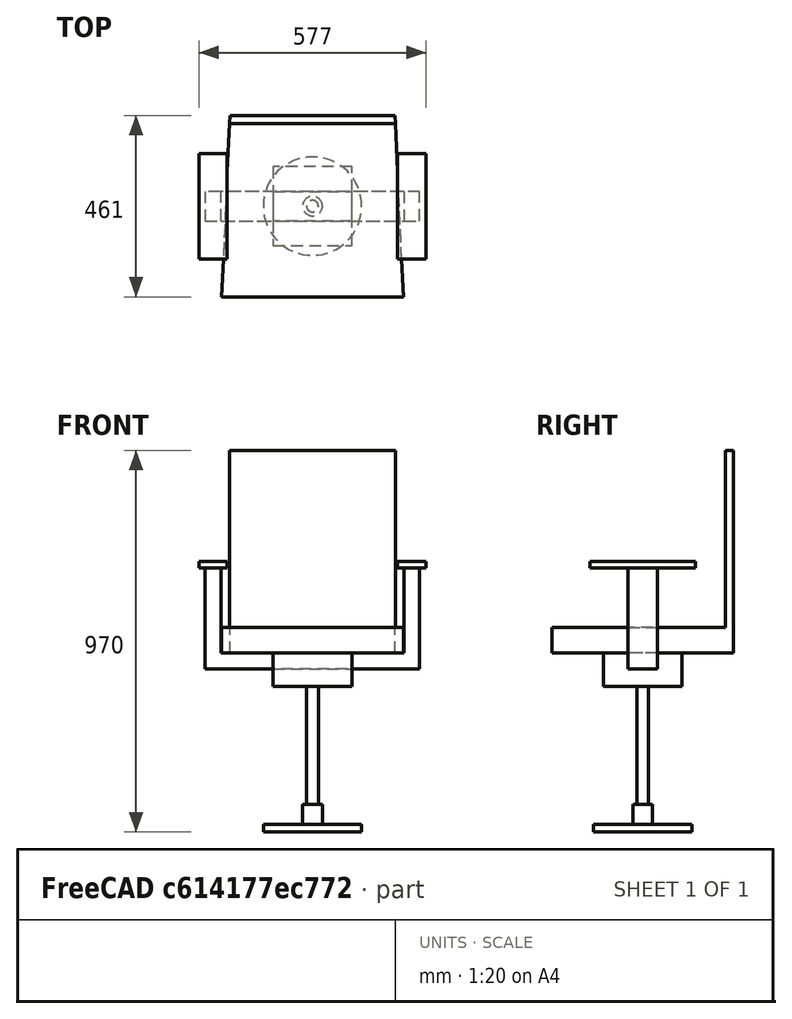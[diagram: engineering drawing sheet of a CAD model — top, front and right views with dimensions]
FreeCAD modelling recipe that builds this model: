
FCSTD DOCUMENT  (FreeCAD 1.0R39109 (Git))
Label: chair02_00501
License: All rights reserved
LicenseURL: https://en.wikipedia.org/wiki/All_rights_reserved
objects: TechDraw::DrawViewDimension×11, Sketcher::SketchObject×10, PartDesign::Pad×10, TechDraw::DrawViewAnnotation×9, PartDesign::Body×5, PartDesign::ShapeBinder×4, TechDraw::DrawSVGTemplate×3, TechDraw::DrawProjGroupItem×3, TechDraw::DrawPage×3, TechDraw::DrawViewSection×3, App::Part×1
note: 79 computed .brp shape members not serialized (recipe doc carries the construction recipe); baked Part::Feature solids carry a one-line shape summary decoded from their .brp

FEATURE [Sketcher::SketchObject] Sketch
  ArcFitTolerance = 1e-06
  AttachmentSupport = -> [XY_Plane]
  FullyConstrained = true
  MakeInternals = false
  MapMode = 5
  sketch-geometry (1):
    g0: Circle CenterX=0 CenterY=0 CenterZ=0 NormalX=0 NormalY=0 NormalZ=1 AngleXU=0 Radius=125
  constraints (2):
    c: Diameter(g0) = 250
    c: Coincident(g0,g-1)
FEATURE [PartDesign::Pad] Pad
  Direction = (0,0,1)
  Length = 20
  Length2 = 10
  Profile = -> Sketch
  ReferenceAxis = -> Sketch [N_Axis]
  Refine = true
  Suppressed = false
  Type = 0
FEATURE [Sketcher::SketchObject] Sketch001
  ArcFitTolerance = 1e-06
  AttachmentSupport = -> [Pad]
  FullyConstrained = true
  MakeInternals = false
  MapMode = 5
  Placement = pos=(0,0,20) rot=(0,0,1;0rad)
  sketch-geometry (1):
    g0: Circle CenterX=0 CenterY=0 CenterZ=0 NormalX=0 NormalY=0 NormalZ=1 AngleXU=0 Radius=25
  constraints (2):
    c: Diameter(g0) = 50
    c: Coincident(g0,g-1)
FEATURE [PartDesign::Pad] Pad001
  BaseFeature = -> Pad
  Direction = (0,0,1)
  Length = 50
  Length2 = 10
  Profile = -> Sketch001
  ReferenceAxis = -> Sketch001 [N_Axis]
  Refine = true
  Suppressed = false
  Type = 0
FEATURE [PartDesign::Body] Body  label="Body1"
  AllowCompound = false
  Group = -> [Sketch,Pad,Sketch001,Pad001]
  Origin = -> Origin
  Tip = -> Pad001
FEATURE [PartDesign::ShapeBinder] CopyPad001  label="Body2_Sketch_P.lane"
  Placement = pos=(0,0,50) rot=(0,0,1;0rad)
  TraceSupport = false
FEATURE [Sketcher::SketchObject] Sketch002
  ArcFitTolerance = 1e-06
  AttachmentSupport = -> [CopyPad001]
  FullyConstrained = true
  MakeInternals = false
  MapMode = 5
  Placement = pos=(0,0,70) rot=(0,0,1;0rad)
  sketch-geometry (1):
    g0: Circle CenterX=0 CenterY=0 CenterZ=0 NormalX=0 NormalY=0 NormalZ=1 AngleXU=0 Radius=15
  constraints (2):
    c: Diameter(g0) = 30
    c: Coincident(g0,g-1)
FEATURE [PartDesign::Pad] Pad002
  Direction = (0,0,1)
  Length = 300
  Length2 = 10
  Placement = pos=(0,0,50) rot=(0,0,1;0rad)
  Profile = -> Sketch002
  ReferenceAxis = -> Sketch002 [N_Axis]
  Refine = true
  Suppressed = false
  Type = 0
FEATURE [PartDesign::Body] Body001  label="Body2"
  AllowCompound = false
  Group = -> [CopyPad001,Sketch002,Pad002]
  Origin = -> Origin001
  Tip = -> Pad002
FEATURE [PartDesign::ShapeBinder] CopyPad002  label="Body3_Sketch_Plane"
  Placement = pos=(0,0,300) rot=(0,0,1;0rad)
  TraceSupport = false
FEATURE [Sketcher::SketchObject] Sketch003
  ArcFitTolerance = 1e-06
  AttachmentSupport = -> [CopyPad002]
  FullyConstrained = true
  MakeInternals = false
  MapMode = 5
  Placement = pos=(0,0,370) rot=(0,0,1;0rad)
  sketch-geometry (5):
    g0: LineSegment StartX=-100 StartY=-100 StartZ=0 EndX=100 EndY=-100 EndZ=0
    g1: LineSegment StartX=100 StartY=-100 StartZ=0 EndX=100 EndY=100 EndZ=0
    g2: LineSegment StartX=100 StartY=100 StartZ=0 EndX=-100 EndY=100 EndZ=0
    g3: LineSegment StartX=-100 StartY=100 StartZ=0 EndX=-100 EndY=-100 EndZ=0
    g4: GeomPoint [constr] X=0 Y=0 Z=0
  constraints (12):
    c: Coincident(g0,g1)
    c: Coincident(g1,g2)
    c: Coincident(g2,g3)
    c: Coincident(g3,g0)
    c: Horizontal(g0)
    c: Horizontal(g2)
    c: Vertical(g1)
    c: Vertical(g3)
    c: Symmetric(g2,g0,g4)
    c: Distance(g1,g3) = 200
    c: Distance(g0,g2) = 200
    c: Coincident(g4,g-1)
FEATURE [PartDesign::Pad] Pad003
  Direction = (0,0,1)
  Length = 45
  Length2 = 10
  Placement = pos=(0,0,300) rot=(0,0,1;0rad)
  Profile = -> Sketch003
  ReferenceAxis = -> Sketch003 [N_Axis]
  Refine = true
  Suppressed = false
  Type = 0
FEATURE [PartDesign::ShapeBinder] CopyPad003  label="Body4_Sketch_Plane"
  Placement = pos=(0,0,45) rot=(0,0,1;0rad)
  TraceSupport = false
FEATURE [Sketcher::SketchObject] Sketch004
  ArcFitTolerance = 1e-06
  AttachmentSupport = -> [CopyPad003]
  FullyConstrained = true
  MakeInternals = false
  MapMode = 5
  Placement = pos=(0,0,415) rot=(0,0,1;0rad)
  sketch-geometry (5):
    g0: LineSegment StartX=-272.5 StartY=-37.5 StartZ=0 EndX=272.5 EndY=-37.5 EndZ=0
    g1: LineSegment StartX=272.5 StartY=-37.5 StartZ=0 EndX=272.5 EndY=37.5 EndZ=0
    g2: LineSegment StartX=272.5 StartY=37.5 StartZ=0 EndX=-272.5 EndY=37.5 EndZ=0
    g3: LineSegment StartX=-272.5 StartY=37.5 StartZ=0 EndX=-272.5 EndY=-37.5 EndZ=0
    g4: GeomPoint [constr] X=0 Y=0 Z=0
  constraints (12):
    c: Coincident(g0,g1)
    c: Coincident(g1,g2)
    c: Coincident(g2,g3)
    c: Coincident(g3,g0)
    c: Horizontal(g0)
    c: Horizontal(g2)
    c: Vertical(g1)
    c: Vertical(g3)
    c: Symmetric(g2,g0,g4)
    c: Distance(g1,g3) = 545
    c: Distance(g0,g2) = 75
    c: Coincident(g4,g-1)
FEATURE [PartDesign::Pad] Pad004
  Direction = (0,0,1)
  Length = 40
  Length2 = 10
  Placement = pos=(0,0,45) rot=(0,0,1;0rad)
  Profile = -> Sketch004
  ReferenceAxis = -> Sketch004 [N_Axis]
  Refine = true
  Suppressed = false
  Type = 0
FEATURE [Sketcher::SketchObject] Sketch005
  ArcFitTolerance = 1e-06
  AttachmentSupport = -> [Pad004]
  ExternalGeometry = -> [Pad004]
  FullyConstrained = true
  MakeInternals = false
  MapMode = 5
  Placement = pos=(0,0,455) rot=(0,0,1;0rad)
  sketch-geometry (8):
    g0: LineSegment StartX=-272.5 StartY=37.5 StartZ=0 EndX=-272.5 EndY=-37.5 EndZ=0
    g1: LineSegment StartX=-272.5 StartY=-37.5 StartZ=0 EndX=-232.5 EndY=-37.5 EndZ=0
    g2: LineSegment StartX=-232.5 StartY=-37.5 StartZ=0 EndX=-232.5 EndY=37.5 EndZ=0
    g3: LineSegment StartX=-232.5 StartY=37.5 StartZ=0 EndX=-272.5 EndY=37.5 EndZ=0
    g4: LineSegment StartX=272.5 StartY=37.5 StartZ=0 EndX=232.5 EndY=37.5 EndZ=0
    g5: LineSegment StartX=232.5 StartY=37.5 StartZ=0 EndX=232.5 EndY=-37.5 EndZ=0
    g6: LineSegment StartX=232.5 StartY=-37.5 StartZ=0 EndX=272.5 EndY=-37.5 EndZ=0
    g7: LineSegment StartX=272.5 StartY=-37.5 StartZ=0 EndX=272.5 EndY=37.5 EndZ=0
  constraints (22):
    c: Coincident(g0,g1)
    c: Coincident(g1,g2)
    c: Coincident(g2,g3)
    c: Coincident(g3,g0)
    c: Vertical(g0)
    c: Vertical(g2)
    c: Horizontal(g1)
    c: Horizontal(g3)
    c: Coincident(g0,g-3)
    c: PointOnObject(g1,g-4)
    c: DistanceX(g3,g3) = 40
    c: Coincident(g4,g5)
    c: Coincident(g5,g6)
    c: Coincident(g6,g7)
    c: Coincident(g7,g4)
    c: Horizontal(g4)
    c: Horizontal(g6)
    c: Vertical(g5)
    c: Vertical(g7)
    c: Coincident(g4,g-3)
    c: PointOnObject(g5,g-4)
    c: Equal(g4,g3)
FEATURE [PartDesign::Pad] Pad005
  BaseFeature = -> Pad004
  Direction = (0,0,1)
  Length = 216
  Length2 = 10
  Placement = pos=(0,0,45) rot=(0,0,1;0rad)
  Profile = -> Sketch005
  ReferenceAxis = -> Sketch005 [N_Axis]
  Refine = true
  Suppressed = false
  Type = 0
FEATURE [Sketcher::SketchObject] Sketch006
  ArcFitTolerance = 1e-06
  AttachmentSupport = -> [Pad005]
  ExternalGeometry = -> [Pad005]
  FullyConstrained = true
  MakeInternals = false
  MapMode = 5
  Placement = pos=(0,0,671) rot=(0,0,1;0rad)
  sketch-geometry (16):
    g0: LineSegment StartX=-288.5 StartY=134 StartZ=0 EndX=-288.5 EndY=-134 EndZ=0
    g1: LineSegment StartX=-288.5 StartY=-134 StartZ=0 EndX=-216.5 EndY=-134 EndZ=0
    g2: LineSegment StartX=-216.5 StartY=-134 StartZ=0 EndX=-216.5 EndY=134 EndZ=0
    g3: LineSegment StartX=-216.5 StartY=134 StartZ=0 EndX=-288.5 EndY=134 EndZ=0
    g4: LineSegment StartX=216.5 StartY=134 StartZ=0 EndX=216.5 EndY=-134 EndZ=0
    g5: LineSegment StartX=216.5 StartY=-134 StartZ=0 EndX=288.5 EndY=-134 EndZ=0
    g6: LineSegment StartX=288.5 StartY=-134 StartZ=0 EndX=288.5 EndY=134 EndZ=0
    g7: LineSegment StartX=288.5 StartY=134 StartZ=0 EndX=216.5 EndY=134 EndZ=0
    g8: LineSegment [constr] StartX=-272.5 StartY=37.5 StartZ=0 EndX=-232.5 EndY=-37.5 EndZ=0
    g9: LineSegment [constr] StartX=-252.5 StartY=0 StartZ=0 EndX=-272.5 EndY=-37.5 EndZ=0
    g10: LineSegment [constr] StartX=232.5 StartY=37.5 StartZ=0 EndX=272.5 EndY=-37.5 EndZ=0
    g11: LineSegment [constr] StartX=272.5 StartY=37.5 StartZ=0 EndX=252.5 EndY=0 EndZ=0
    g12: LineSegment [constr] StartX=-216.5 StartY=134 StartZ=0 EndX=-288.5 EndY=-134 EndZ=0
    g13: LineSegment [constr] StartX=-288.5 StartY=134 StartZ=0 EndX=-252.5 EndY=0 EndZ=0
    g14: LineSegment [constr] StartX=216.5 StartY=134 StartZ=0 EndX=288.5 EndY=-134 EndZ=0
    g15: LineSegment [constr] StartX=288.5 StartY=134 StartZ=0 EndX=252.5 EndY=0 EndZ=0
  constraints (38):
    c: Coincident(g0,g1)
    c: Coincident(g1,g2)
    c: Coincident(g2,g3)
    c: Coincident(g3,g0)
    c: Vertical(g0)
    c: Vertical(g2)
    c: Horizontal(g1)
    c: Horizontal(g3)
    c: Coincident(g4,g5)
    c: Coincident(g5,g6)
    c: Coincident(g6,g7)
    c: Coincident(g7,g4)
    c: Vertical(g4)
    c: Vertical(g6)
    c: Horizontal(g5)
    c: Horizontal(g7)
    c: Equal(g7,g3)
    c: Equal(g2,g4)
    c: DistanceX(g3,g3) = 72
    c: Coincident(g8,g-4)
    c: Coincident(g8,g-3)
    c: Coincident(g9,g-4)
    c: Coincident(g10,g-5)
    c: Coincident(g10,g-6)
    c: Coincident(g11,g-6)
    c: Symmetric(g10,g10,g11)
    c: Symmetric(g8,g8,g9)
    c: Coincident(g12,g2)
    c: Coincident(g12,g0)
    c: Coincident(g13,g0)
    c: Symmetric(g12,g12,g13)
    c: Coincident(g9,g13)
    c: Coincident(g14,g4)
    c: Coincident(g14,g5)
    c: Coincident(g15,g6)
    c: Symmetric(g14,g14,g15)
    c: Coincident(g15,g11)
    c: DistanceY(g2,g2) = 268
FEATURE [PartDesign::Pad] Pad006
  BaseFeature = -> Pad005
  Direction = (0,0,1)
  Length = 17
  Length2 = 10
  Placement = pos=(0,0,45) rot=(0,0,1;0rad)
  Profile = -> Sketch006
  ReferenceAxis = -> Sketch006 [N_Axis]
  Refine = true
  Suppressed = false
  Type = 0
FEATURE [PartDesign::Body] Body003  label="Body4"
  AllowCompound = false
  Group = -> [CopyPad003,Sketch004,Pad004,Sketch005,Pad005,Sketch006,Pad006]
  Origin = -> Origin003
  Tip = -> Pad006
FEATURE [PartDesign::ShapeBinder] CopyPad006  label="Body5_Sketch_Plane"
  Placement = pos=(0,0,45) rot=(0,0,1;0rad)
  TraceSupport = false
FEATURE [Sketcher::SketchObject] Sketch009
  ArcFitTolerance = 1e-06
  AttachmentSupport = -> [Pad003]
  ExternalGeometry = -> [Pad003]
  FullyConstrained = true
  MakeInternals = false
  MapMode = 5
  Placement = pos=(0,0,415) rot=(0,0,1;0rad)
  sketch-geometry (8):
    g0: LineSegment StartX=-100 StartY=100 StartZ=0 EndX=-100 EndY=37.5 EndZ=0
    g1: LineSegment StartX=-100 StartY=37.5 StartZ=0 EndX=100 EndY=37.5 EndZ=0
    g2: LineSegment StartX=100 StartY=37.5 StartZ=0 EndX=100 EndY=100 EndZ=0
    g3: LineSegment StartX=100 StartY=100 StartZ=0 EndX=-100 EndY=100 EndZ=0
    g4: LineSegment StartX=100 StartY=-100 StartZ=0 EndX=100 EndY=-37.5 EndZ=0
    g5: LineSegment StartX=100 StartY=-37.5 StartZ=0 EndX=-100 EndY=-37.5 EndZ=0
    g6: LineSegment StartX=-100 StartY=-37.5 StartZ=0 EndX=-100 EndY=-100 EndZ=0
    g7: LineSegment StartX=-100 StartY=-100 StartZ=0 EndX=100 EndY=-100 EndZ=0
  constraints (21):
    c: Coincident(g0,g1)
    c: Coincident(g1,g2)
    c: Coincident(g2,g3)
    c: Coincident(g3,g0)
    c: Vertical(g0)
    c: Vertical(g2)
    c: Horizontal(g1)
    c: Horizontal(g3)
    c: Coincident(g0,g-3)
    c: PointOnObject(g1,g-4)
    c: Coincident(g4,g5)
    c: Coincident(g5,g6)
    c: Coincident(g6,g7)
    c: Coincident(g7,g4)
    c: Vertical(g6)
    c: Horizontal(g5)
    c: Horizontal(g7)
    c: Coincident(g4,g-4)
    c: PointOnObject(g5,g-3)
    c: DistanceY(g4,g1) = 75
    c: Symmetric(g1,g4,g-1)
FEATURE [PartDesign::Pad] Pad009
  BaseFeature = -> Pad003
  Direction = (0,0,1)
  Length = 40
  Length2 = 10
  Placement = pos=(0,0,300) rot=(0,0,1;0rad)
  Profile = -> Sketch009
  ReferenceAxis = -> Sketch009 [N_Axis]
  Refine = true
  Suppressed = false
  Type = 0
FEATURE [PartDesign::Body] Body002  label="Body3"
  AllowCompound = false
  Group = -> [CopyPad002,Sketch003,Pad003,Sketch009,Pad009]
  Origin = -> Origin002
  Tip = -> Pad009
FEATURE [Sketcher::SketchObject] Sketch007
  ArcFitTolerance = 1e-06
  AttachmentSupport = -> [CopyPad006]
  FullyConstrained = true
  MakeInternals = false
  MapMode = 5
  Placement = pos=(0,0,455) rot=(0,0,1;0rad)
  sketch-geometry (8):
    g0: LineSegment StartX=-210 StartY=230.5 StartZ=0 EndX=-231 EndY=-230.5 EndZ=0
    g1: LineSegment StartX=-231 StartY=-230.5 StartZ=0 EndX=231 EndY=-230.5 EndZ=0
    g2: LineSegment StartX=231 StartY=-230.5 StartZ=0 EndX=210 EndY=230.5 EndZ=0
    g3: LineSegment StartX=210 StartY=230.5 StartZ=0 EndX=-210 EndY=230.5 EndZ=0
    g4: LineSegment [constr] StartX=210 StartY=230.5 StartZ=0 EndX=2.84e-14 EndY=0 EndZ=0
    g5: LineSegment [constr] StartX=2.84e-14 StartY=0 StartZ=0 EndX=-210 EndY=230.5 EndZ=0
    g6: LineSegment [constr] StartX=210 StartY=230.5 StartZ=0 EndX=210 EndY=0 EndZ=0
    g7: LineSegment [constr] StartX=231 StartY=-230.5 StartZ=0 EndX=231 EndY=0 EndZ=0
  constraints (20):
    c: Coincident(g2,g1)
    c: DistanceX(g1,g1) = 462
    c: DistanceX(g3,g3) = 420
    c: Coincident(g1,g0)
    c: Symmetric(g2,g0,g-2)
    c: Coincident(g2,g3)
    c: Coincident(g3,g0)
    c: Coincident(g4,g2)
    c: Coincident(g4,g-1)
    c: Coincident(g5,g4)
    c: Coincident(g5,g0)
    c: DistanceY(g2,g2) = 461
    c: Coincident(g6,g2)
    c: PointOnObject(g6,g-1)
    c: Vertical(g6)
    c: Coincident(g7,g1)
    c: PointOnObject(g7,g-1)
    c: Vertical(g7)
    c: Equal(g7,g6)
    c: Symmetric(g1,g0,g-2)
FEATURE [PartDesign::Pad] Pad007
  Direction = (0,0,1)
  Length = 65
  Length2 = 10
  Placement = pos=(0,0,45) rot=(0,0,1;0rad)
  Profile = -> Sketch007
  ReferenceAxis = -> Sketch007 [N_Axis]
  Refine = true
  Suppressed = false
  Type = 0
FEATURE [Sketcher::SketchObject] Sketch008
  ArcFitTolerance = 1e-06
  AttachmentSupport = -> [Pad007]
  ExternalGeometry = -> [Pad007]
  FullyConstrained = true
  MakeInternals = false
  MapMode = 5
  Placement = pos=(0,0,520) rot=(0,0,1;0rad)
  sketch-geometry (4):
    g0: LineSegment StartX=-210 StartY=230.5 StartZ=0 EndX=210 EndY=230.5 EndZ=0
    g1: LineSegment StartX=-210 StartY=230.5 StartZ=0 EndX=-210.957 EndY=209.5 EndZ=0
    g2: LineSegment StartX=-210.957 StartY=209.5 StartZ=0 EndX=210.957 EndY=209.5 EndZ=0
    g3: LineSegment StartX=210 StartY=230.5 StartZ=0 EndX=210.957 EndY=209.5 EndZ=0
  constraints (10):
    c: Coincident(g0,g-3)
    c: Coincident(g0,g-4)
    c: Coincident(g1,g0)
    c: PointOnObject(g1,g-3)
    c: Coincident(g2,g1)
    c: PointOnObject(g2,g-4)
    c: Horizontal(g2)
    c: Coincident(g3,g0)
    c: Coincident(g3,g2)
    c: DistanceY(g1,g1) = 21
FEATURE [PartDesign::Pad] Pad008
  BaseFeature = -> Pad007
  Direction = (0,0,1)
  Length = 450
  Length2 = 10
  Placement = pos=(0,0,45) rot=(0,0,1;0rad)
  Profile = -> Sketch008
  ReferenceAxis = -> Sketch008 [N_Axis]
  Refine = true
  Suppressed = false
  Type = 0
FEATURE [PartDesign::Body] Body004  label="Body5"
  AllowCompound = false
  Group = -> [CopyPad006,Sketch007,Pad007,Sketch008,Pad008]
  Origin = -> Origin004
  Tip = -> Pad008
FEATURE [App::Part] Part  label="chair02"
  Group = -> [Body,Body001,Body002,Body003,Body004]
  Origin = -> Origin005
FEATURE [TechDraw::DrawSVGTemplate] Template  label="テンプレート"
  Height = 210
  Orientation = 1
  Template = <userpath>/AppData/Local/Programs/FreeCAD 1.0/data/Mod/TechDraw/Templates/A4_Landscape_blank.svg
  Width = 297
FEATURE [TechDraw::DrawProjGroupItem] View
  CoarseView = false
  Direction = (0,0,1)
  Focus = 100
  HardHidden = true
  IsoCount = 0
  IsoHidden = false
  IsoVisible = false
  LockPosition = false
  Perspective = false
  Rotation = 0
  RotationVector = (1,0,0)
  Scale = 0.333333
  ScaleType = 2
  ScrubCount = 1
  SeamHidden = false
  SeamVisible = false
  SmoothHidden = false
  SmoothVisible = true
  Source = -> [Part]
  Type = 0
  X = 131.425
  XDirection = (1,0,0)
  Y = 107.897
FEATURE [TechDraw::DrawViewDimension] Dimension  label="寸法"
  AngleOverride = false
  Arbitrary = false
  ArbitraryTolerances = false
  BoxCorners = (2) [(-96.1666,-76.8333,0),(96.1666,76.8333,0)]
  EqualTolerance = true
  ExtensionAngle = 0
  FormatSpec = %.2w
  FormatSpecOverTolerance = %+.2w
  FormatSpecUnderTolerance = %+.2w
  Inverted = false
  LineAngle = 0
  LockPosition = false
  MeasureType = 1
  OverTolerance = 0
  References2D = -> [View]
  Rotation = 0
  Scale = 0.2
  ScaleType = 2
  TheoreticalExact = false
  Type = 1
  UnderTolerance = 0
  X = 0
  Y = 93.9298
FEATURE [TechDraw::DrawViewDimension] Dimension001  label="寸法001"
  AngleOverride = false
  Arbitrary = false
  ArbitraryTolerances = false
  BoxCorners = (2) [(-96.1666,-76.8333,0),(96.1666,76.8333,0)]
  EqualTolerance = true
  ExtensionAngle = 0
  FormatSpec = %.2w
  FormatSpecOverTolerance = %+.2w
  FormatSpecUnderTolerance = %+.2w
  Inverted = false
  LineAngle = 0
  LockPosition = false
  MeasureType = 1
  OverTolerance = 0
  References2D = -> [View]
  Rotation = 0
  Scale = 0.2
  ScaleType = 2
  TheoreticalExact = false
  Type = 2
  UnderTolerance = 0
  X = 135.701
  Y = 0
FEATURE [TechDraw::DrawViewDimension] Dimension002  label="寸法002"
  AngleOverride = false
  Arbitrary = false
  ArbitraryTolerances = false
  BoxCorners = (2) [(-96.1666,-76.8333,0),(96.1666,76.8333,0)]
  EqualTolerance = true
  ExtensionAngle = 0
  FormatSpec = %.2w
  FormatSpecOverTolerance = %+.2w
  FormatSpecUnderTolerance = %+.2w
  Inverted = false
  LineAngle = 0
  LockPosition = false
  MeasureType = 1
  OverTolerance = 0
  References2D = -> [View]
  Rotation = 0
  Scale = 0.2
  ScaleType = 2
  TheoreticalExact = false
  Type = 2
  UnderTolerance = 0
  X = 113.57
  Y = 61.6706
FEATURE [TechDraw::DrawViewDimension] Dimension003  label="寸法003"
  AngleOverride = false
  Arbitrary = false
  ArbitraryTolerances = false
  BoxCorners = (2) [(-96.1666,-76.8333,0),(96.1666,76.8333,0)]
  EqualTolerance = true
  ExtensionAngle = 0
  FormatSpec = %.2w
  FormatSpecOverTolerance = %+.2w
  FormatSpecUnderTolerance = %+.2w
  Inverted = false
  LineAngle = 0
  LockPosition = false
  MeasureType = 1
  OverTolerance = 0
  References2D = -> [View]
  Rotation = 0
  Scale = 0.2
  ScaleType = 2
  TheoreticalExact = false
  Type = 2
  UnderTolerance = 0
  X = 125.233
  Y = 0.063601
FEATURE [TechDraw::DrawViewDimension] Dimension004  label="寸法004"
  AngleOverride = false
  Arbitrary = false
  ArbitraryTolerances = false
  BoxCorners = (2) [(-96.1666,-76.8333,0),(96.1666,76.8333,0)]
  EqualTolerance = true
  ExtensionAngle = 0
  FormatSpec = %.2w
  FormatSpecOverTolerance = %+.2w
  FormatSpecUnderTolerance = %+.2w
  Inverted = false
  LineAngle = 0
  LockPosition = false
  MeasureType = 1
  OverTolerance = 0
  References2D = -> [View]
  Rotation = 0
  Scale = 0.2
  ScaleType = 2
  TheoreticalExact = false
  Type = 1
  UnderTolerance = 0
  X = -84.1666
  Y = 58.5053
FEATURE [TechDraw::DrawViewDimension] Dimension005  label="寸法005"
  AngleOverride = false
  Arbitrary = false
  ArbitraryTolerances = false
  BoxCorners = (2) [(-96.1666,-76.8333,0),(96.1666,76.8333,0)]
  EqualTolerance = true
  ExtensionAngle = 0
  FormatSpec = %.2w
  FormatSpecOverTolerance = %+.2w
  FormatSpecUnderTolerance = %+.2w
  Inverted = false
  LineAngle = 0
  LockPosition = false
  MeasureType = 1
  OverTolerance = 0
  References2D = -> [View]
  Rotation = 0
  Scale = 0.2
  ScaleType = 2
  TheoreticalExact = false
  Type = 2
  UnderTolerance = 0
  X = -108.801
  Y = 0
FEATURE [TechDraw::DrawViewDimension] Dimension006  label="寸法006"
  AngleOverride = false
  Arbitrary = false
  ArbitraryTolerances = false
  BoxCorners = (2) [(-96.1666,-76.8333,0),(96.1666,76.8333,0)]
  EqualTolerance = true
  ExtensionAngle = 0
  FormatSpec = %.2w
  FormatSpecOverTolerance = %+.2w
  FormatSpecUnderTolerance = %+.2w
  Inverted = false
  LineAngle = 0
  LockPosition = false
  MeasureType = 1
  OverTolerance = 0
  References2D = -> [View]
  Rotation = 0
  Scale = 0.2
  ScaleType = 2
  TheoreticalExact = false
  Type = 1
  UnderTolerance = 0
  X = 0
  Y = -83.8244
FEATURE [TechDraw::DrawPage] Page  label="用紙"
  KeepUpdated = true
  NextBalloonIndex = 1
  ProjectionType = 0
  Template = -> Template
  Views = -> [View,Dimension,Dimension001,Dimension002,Dimension003,Dimension004,Dimension005,Dimension006]
FEATURE [TechDraw::DrawSVGTemplate] Template001  label="テンプレート001"
  Height = 210
  Orientation = 1
  Template = <userpath>/AppData/Local/Programs/FreeCAD 1.0/data/Mod/TechDraw/Templates/A4_Landscape_blank.svg
  Width = 297
FEATURE [TechDraw::DrawSVGTemplate] Template002  label="テンプレート002"
  Height = 210
  Orientation = 1
  Template = <userpath>/AppData/Local/Programs/FreeCAD 1.0/data/Mod/TechDraw/Templates/A4_Landscape_blank.svg
  Width = 297
FEATURE [TechDraw::DrawProjGroupItem] View001
  CoarseView = false
  Direction = (0,-1,0)
  Focus = 100
  HardHidden = true
  IsoCount = 0
  IsoHidden = false
  IsoVisible = false
  LockPosition = false
  Perspective = false
  Rotation = 0
  RotationVector = (1,0,0)
  Scale = 0.2
  ScaleType = 2
  ScrubCount = 1
  SeamHidden = false
  SeamVisible = false
  SmoothHidden = false
  SmoothVisible = true
  Source = -> [Part]
  Type = 0
  X = 72.2264
  XDirection = (1,0,0)
  Y = 108.632
FEATURE [TechDraw::DrawViewSection] SectionView  label="セクション  - "
  BaseView = -> View001
  CoarseView = false
  CutSurfaceDisplay = 2
  Direction = (1e-16,0,1)
  FileGeomPattern = <userpath>\AppData\Local\Programs\FreeCAD 1.0\data\Mod/TechDraw/PAT/FCPAT.pat
  FileHatchPattern = <userpath>\AppData\Local\Programs\FreeCAD 1.0\data\Mod/TechDraw/Patterns/simple.svg
  Focus = 100
  FuseBeforeCut = false
  HardHidden = true
  HatchOffset = (0,0,0)
  HatchRotation = 0
  HatchScale = 1
  IsoCount = 0
  IsoHidden = false
  IsoVisible = false
  LockPosition = false
  NameGeomPattern = Diamond
  Perspective = false
  Rotation = 0
  Scale = 0.15
  ScaleType = 2
  ScrubCount = 1
  SeamHidden = false
  SeamVisible = false
  SectionDirection = 4
  SectionLineStretch = 1
  SectionNormal = (1e-16,0,1)
  SectionOrigin = (0,0,581)
  SmoothHidden = false
  SmoothVisible = true
  Source = -> [Part]
  TrimAfterCut = false
  UsePreviousCut = false
  X = 215.858
  XDirection = (1,0,-1e-16)
  Y = 166.085
FEATURE [TechDraw::DrawViewSection] SectionView001  label="セクション001  - "
  BaseView = -> View001
  CoarseView = false
  CutSurfaceDisplay = 2
  Direction = (1e-16,0,1)
  FileGeomPattern = <userpath>\AppData\Local\Programs\FreeCAD 1.0\data\Mod/TechDraw/PAT/FCPAT.pat
  FileHatchPattern = <userpath>\AppData\Local\Programs\FreeCAD 1.0\data\Mod/TechDraw/Patterns/simple.svg
  Focus = 100
  FuseBeforeCut = false
  HardHidden = true
  HatchOffset = (0,0,0)
  HatchRotation = 0
  HatchScale = 1
  IsoCount = 0
  IsoHidden = false
  IsoVisible = false
  LockPosition = false
  NameGeomPattern = Diamond
  Perspective = false
  Rotation = 0
  Scale = 0.15
  ScaleType = 2
  ScrubCount = 1
  SeamHidden = false
  SeamVisible = false
  SectionDirection = 4
  SectionLineStretch = 1
  SectionNormal = (1e-16,0,1)
  SectionOrigin = (0,0,437)
  SmoothHidden = false
  SmoothVisible = true
  Source = -> [Part]
  TrimAfterCut = false
  UsePreviousCut = false
  X = 215.086
  XDirection = (1,0,-1e-16)
  Y = 92.3168
FEATURE [TechDraw::DrawViewSection] SectionView002  label="セクション002  - "
  BaseView = -> View001
  CoarseView = false
  CutSurfaceDisplay = 2
  Direction = (1e-16,0,1)
  FileGeomPattern = <userpath>\AppData\Local\Programs\FreeCAD 1.0\data\Mod/TechDraw/PAT/FCPAT.pat
  FileHatchPattern = <userpath>\AppData\Local\Programs\FreeCAD 1.0\data\Mod/TechDraw/Patterns/simple.svg
  Focus = 100
  FuseBeforeCut = false
  HardHidden = true
  HatchOffset = (0,0,0)
  HatchRotation = 0
  HatchScale = 1
  IsoCount = 0
  IsoHidden = false
  IsoVisible = false
  LockPosition = false
  NameGeomPattern = Diamond
  Perspective = false
  Rotation = 0
  Scale = 0.15
  ScaleType = 2
  ScrubCount = 1
  SeamHidden = false
  SeamVisible = false
  SectionDirection = 4
  SectionLineStretch = 1
  SectionNormal = (1e-16,0,1)
  SectionOrigin = (0,0,200)
  SmoothHidden = false
  SmoothVisible = true
  Source = -> [Part]
  TrimAfterCut = false
  UsePreviousCut = false
  X = 214.868
  XDirection = (1,0,-1e-16)
  Y = 24.434
FEATURE [TechDraw::DrawViewDimension] Dimension014  label="寸法014"
  AngleOverride = false
  Arbitrary = false
  ArbitraryTolerances = false
  BoxCorners = (2) [(-18.75,-18.75,0),(18.75,18.75,0)]
  EqualTolerance = true
  ExtensionAngle = 0
  FormatSpec = ⌀%.2w
  FormatSpecOverTolerance = %+.2w
  FormatSpecUnderTolerance = %+.2w
  Inverted = false
  LineAngle = 0
  LockPosition = false
  MeasureType = 1
  OverTolerance = 0
  References2D = -> [SectionView002]
  Rotation = 0
  Scale = 0.2
  ScaleType = 2
  TheoreticalExact = false
  Type = 5
  UnderTolerance = 0
  X = 10.9229
  Y = 0.736379
FEATURE [TechDraw::DrawViewDimension] Dimension015  label="寸法015"
  AngleOverride = false
  Arbitrary = false
  ArbitraryTolerances = false
  BoxCorners = (2) [(-18.75,-18.75,0),(18.75,18.75,0)]
  EqualTolerance = true
  ExtensionAngle = 0
  FormatSpec = ⌀%.2w
  FormatSpecOverTolerance = %+.2w
  FormatSpecUnderTolerance = %+.2w
  Inverted = false
  LineAngle = 0
  LockPosition = false
  MeasureType = 1
  OverTolerance = 0
  References2D = -> [SectionView002]
  Rotation = 0
  Scale = 0.2
  ScaleType = 2
  TheoreticalExact = false
  Type = 5
  UnderTolerance = 0
  X = 22.705
  Y = 18.6549
FEATURE [TechDraw::DrawViewAnnotation] Annotation  label="注釈"
  Font = osifont
  LineSpace = 100
  LockPosition = false
  MaxWidth = -1
  Rotation = 0
  Scale = 0.2
  ScaleType = 2
  Text = A
  TextSize = 5
  TextStyle = 0
  X = 143.937
  Y = 118.99
FEATURE [TechDraw::DrawViewAnnotation] Annotation001  label="注釈001"
  Font = osifont
  LineSpace = 100
  LockPosition = false
  MaxWidth = -1
  Rotation = 0
  Scale = 0.2
  ScaleType = 2
  Text = A
  TextSize = 5
  TextStyle = 0
  X = 9.25009
  Y = 118.99
FEATURE [TechDraw::DrawViewAnnotation] Annotation002  label="注釈002"
  Font = osifont
  LineSpace = 100
  LockPosition = false
  MaxWidth = -1
  Rotation = 0
  Scale = 0.2
  ScaleType = 2
  Text = B
  TextSize = 5
  TextStyle = 0
  X = 9.25009
  Y = 89.4351
FEATURE [TechDraw::DrawViewAnnotation] Annotation003  label="注釈003"
  Font = osifont
  LineSpace = 100
  LockPosition = false
  MaxWidth = -1
  Rotation = 0
  Scale = 0.2
  ScaleType = 2
  Text = B
  TextSize = 5
  TextStyle = 0
  X = 145.458
  Y = 89.4351
FEATURE [TechDraw::DrawViewAnnotation] Annotation004  label="注釈004"
  Font = osifont
  LineSpace = 100
  LockPosition = false
  MaxWidth = -1
  Rotation = 0
  Scale = 0.2
  ScaleType = 2
  Text = C
  TextSize = 5
  TextStyle = 0
  X = 145.458
  Y = 40.7495
FEATURE [TechDraw::DrawViewAnnotation] Annotation005  label="注釈005"
  Font = osifont
  LineSpace = 100
  LockPosition = false
  MaxWidth = -1
  Rotation = 0
  Scale = 0.2
  ScaleType = 2
  Text = C
  TextSize = 5
  TextStyle = 0
  X = 9.25009
  Y = 43.6474
FEATURE [TechDraw::DrawViewAnnotation] Annotation006  label="注釈006"
  Font = osifont
  LineSpace = 100
  LockPosition = false
  MaxWidth = -1
  Rotation = 0
  Scale = 0.2
  ScaleType = 2
  Text = A-A
  TextSize = 5
  TextStyle = 0
  X = 215.858
  Y = 205.891
FEATURE [TechDraw::DrawViewAnnotation] Annotation007  label="注釈007"
  Font = osifont
  LineSpace = 100
  LockPosition = false
  MaxWidth = -1
  Rotation = 0
  Scale = 0.2
  ScaleType = 2
  Text = B-B
  TextSize = 5
  TextStyle = 0
  X = 215.858
  Y = 117.871
FEATURE [TechDraw::DrawViewAnnotation] Annotation008  label="注釈008"
  Font = osifont
  LineSpace = 100
  LockPosition = false
  MaxWidth = -1
  Rotation = 0
  Scale = 0.2
  ScaleType = 2
  Text = C -C
  TextSize = 5
  TextStyle = 0
  X = 215.858
  Y = 48.4539
FEATURE [TechDraw::DrawPage] Page002  label="用紙002"
  KeepUpdated = true
  NextBalloonIndex = 1
  ProjectionType = 0
  Template = -> Template002
  Views = -> [View001,SectionView,SectionView001,SectionView002,Dimension014,Dimension015,Annotation,Annotation001,Annotation002,Annotation003,Annotation004,Annotation005,Annotation006,Annotation007,Annotation008]
FEATURE [TechDraw::DrawProjGroupItem] View002
  CoarseView = false
  Direction = (0,-1,0)
  Focus = 100
  HardHidden = true
  IsoCount = 0
  IsoHidden = false
  IsoVisible = false
  LockPosition = false
  Perspective = false
  Rotation = 0
  RotationVector = (1,0,0)
  Scale = 0.2
  ScaleType = 2
  ScrubCount = 1
  SeamHidden = false
  SeamVisible = false
  SmoothHidden = false
  SmoothVisible = true
  Source = -> [Part]
  Type = 0
  X = 144.274
  XDirection = (1,0,0)
  Y = 104.736
FEATURE [TechDraw::DrawViewDimension] Dimension025  label="寸法025"
  AngleOverride = false
  Arbitrary = false
  ArbitraryTolerances = false
  BoxCorners = (2) [(-48.0834,-80.8335,-1e-07),(48.0834,80.8335,1e-07)]
  EqualTolerance = true
  ExtensionAngle = 0
  FormatSpec = %.2w
  FormatSpecOverTolerance = %+.2w
  FormatSpecUnderTolerance = %+.2w
  Inverted = false
  LineAngle = 0
  LockPosition = false
  MeasureType = 1
  OverTolerance = 0
  References2D = -> [View002]
  Rotation = 0
  Scale = 0.2
  ScaleType = 2
  TheoreticalExact = false
  Type = 0
  UnderTolerance = 0
  X = 44.6521
  Y = -73.3335
FEATURE [TechDraw::DrawViewDimension] Dimension026  label="寸法026"
  AngleOverride = false
  Arbitrary = false
  ArbitraryTolerances = false
  BoxCorners = (2) [(-48.0834,-80.8335,-1e-07),(48.0834,80.8335,1e-07)]
  EqualTolerance = true
  ExtensionAngle = 0
  FormatSpec = %.2w
  FormatSpecOverTolerance = %+.2w
  FormatSpecUnderTolerance = %+.2w
  Inverted = false
  LineAngle = 0
  LockPosition = false
  MeasureType = 1
  OverTolerance = 0
  References2D = -> [View002]
  Rotation = 0
  Scale = 0.2
  ScaleType = 2
  TheoreticalExact = false
  Type = 0
  UnderTolerance = 0
  X = 30.6063
  Y = -88.96
FEATURE [TechDraw::DrawPage] Page001  label="用紙001"
  KeepUpdated = true
  NextBalloonIndex = 1
  ProjectionType = 0
  Template = -> Template001
  Views = -> [View002,Dimension025,Dimension026]
